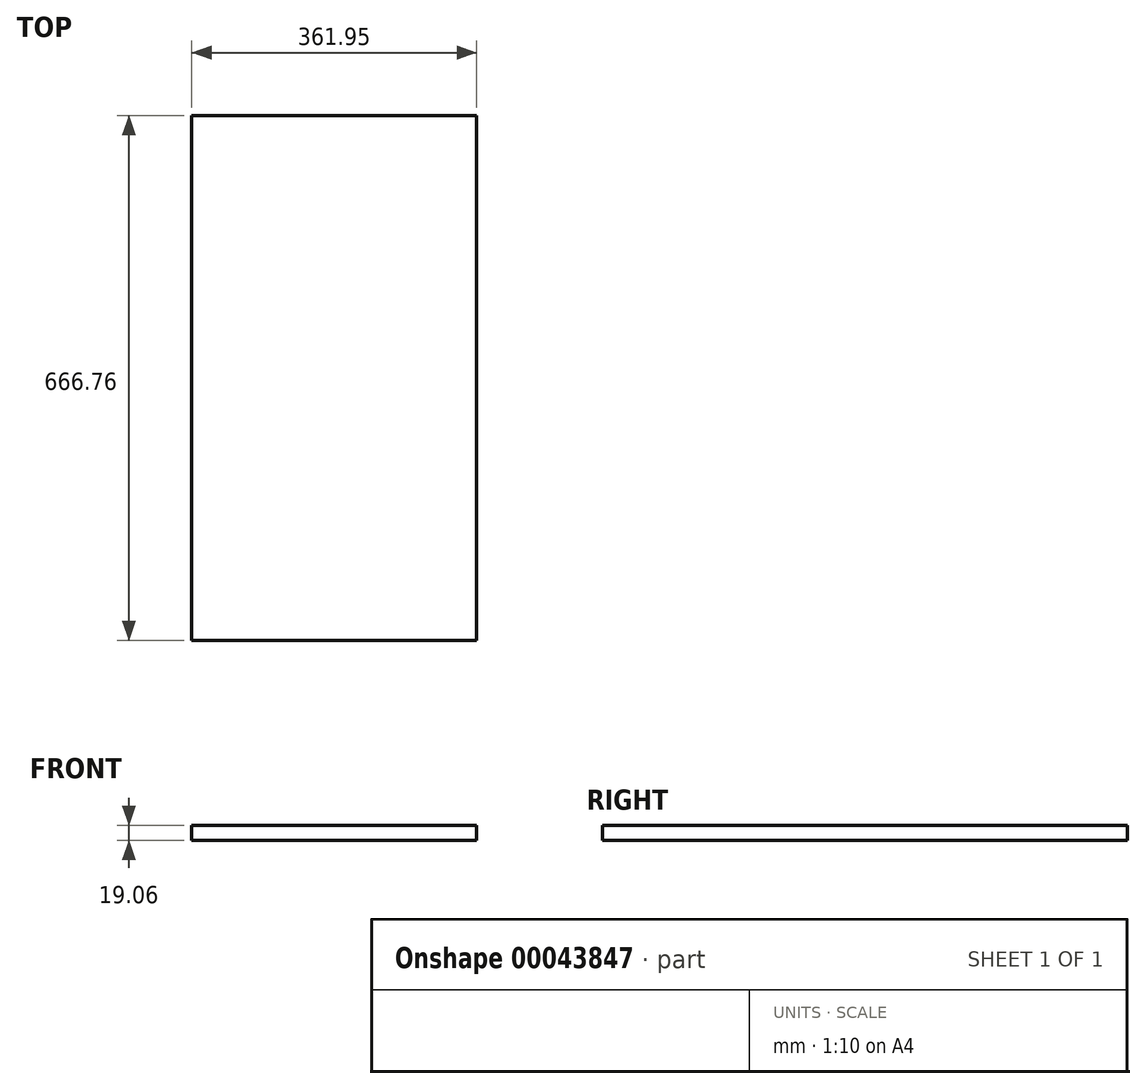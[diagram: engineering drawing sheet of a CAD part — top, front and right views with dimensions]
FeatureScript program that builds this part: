
annotation { "Feature Type Name" : "Feature", "Feature Type Description" : "" }
export const myFeature = defineFeature(function(context is Context, id is Id, definition is map)
    precondition{}
    {
        {
            var Q0;
            Q0=qCreatedBy(makeId("Right.planeOp"),FACE);
            var sketch = newSketch(context, id + "F0", { "sketchPlane" : qUnion([Q0])});
            skLineSegment(sketch, "E0.rect.bottom", {"start": v(333.38, -9.52) * mm, "end": v(-333.38, -9.53) * mm});
            skLineSegment(sketch, "E0.rect.top", {"start": v(333.38, 9.52) * mm, "end": v(-333.38, 9.52) * mm});
            skLineSegment(sketch, "E0.rect.left", {"start": v(333.38, -9.52) * mm, "end": v(333.38, 9.53) * mm});
            skLineSegment(sketch, "E0.rect.right", {"start": v(-333.38, -9.53) * mm, "end": v(-333.38, 9.53) * mm});
            skPoint(sketch, "E0.rect.middle", {"position": v(0, 0) * mm});
            skSolve(sketch);
        }
        {
            var Q0;
            Q0=makeQuery(id+"F0.imprint","IMPRINT",FACE,{"disambiguationData":[TD([[makeQuery(id+"F0.imprint","IMPRINT",EDGE,{"derivedFrom":sQuery(id+"F0.wireOp",EDGE,"E0.rect.bottom")}),-1.0]])]});
            extrude(context, id + "F1", {"entities" : qUnion([Q0]), "depth" : 361.95 * mm});
        }
    });
